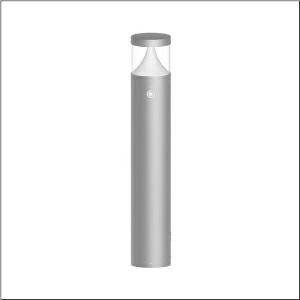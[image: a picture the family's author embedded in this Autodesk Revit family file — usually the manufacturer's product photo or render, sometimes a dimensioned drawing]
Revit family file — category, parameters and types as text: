
# Revit family: cl_31_poller_90_sensor_5cl444803
name_source: partatom
category: Lighting Fixtures
units: mm (PartAtom-declared; Revit-internal decimal feet)

## family parameters
Cut with Voids When Loaded = No
Host = Face
Light Source = No
Part Type = Normal
Room Calculation Point = No
Round Connector Dimension = Use Diameter
Shared = No

## types (1)
- --- (1 x LED, 1500 lm, 14 W, 3000K)
    Apparent Load = 14 VA
    CIE Flux Codes = 19 66 88 92 100
    Color Rendering = 80
    Color Temperature = 3000K
    Default Elevation = 1800 mm
    Description = CL 31 Bollard 90 Sensor, bollard luminaire, primary light control with lens, of PC, primary optical cover: cover panel, of PC, transparent, secondary light control with reflector, of PC, primary light characteristic: asymmetric, LED, rated luminous flux: 1.500lm, luminous efficacy: 107lm/W, light colour: 830, colour temperature: 3000K, control gear: ECG DALI, with terminal, 5-pole, max. 2.5mm², mains connection: 220..240V, AC, 50/60Hz, rated input power: 14W, luminaire housing, of aluminium, powder-coated, Siteco® metallic grey, diameter: 170mm, height: 900mm, PIR sensor, protection rating (complete): IP65, insulation class (complete): insulation class I (protective earthing), certification: CE, ENEC, impact resistance: IK08, permissible operating ambient temperature for outdoor applications: -20..+50°C, packaging unit: 1 piece
    Height = 200 mm  [stored 0.656168 ft]
    Lamp = 1 x LED
    Lamp Light Flux = 1500 lm
    Lamp Power = 14 W
    Lamp count = 1
    Length = 170 mm  [stored 0.557743 ft]
    Luminous efficacy = 107 lm/W
    Manufacturer = Siteco
    ModVariant = No
    Model = 5CL444803
    Mounting Place = Floor
    Mounting Type = Freestanding
    Number of Poles = 1
    OnlyDefault = Yes
    Power Factor = 1
    Product Name = CL 31 Poller 90 Sensor
    Product group = bollard luminaire
    ProductGroupID = 1304
    Protection Class = Protection class I
    Protection Degree = IP 65
    RLX_Detail_Level = 1
    RLX_Emergency_Light_Flux = 0 lm
    RLX_Emergency_Type = 0
    RLX_Emergency_Type_DB = No
    RlxData = <blob elided: 65617 chars, md5=5af5fd18>
    Socket = socket
    Standby Power = 0 W
    System Light Flux = 1500 lm
    System Power = 14 W
    Type Comments = factory setting: luminous flux: 100 % | dim-lin: 254 | 350 mA
    Type Image = l_1006897.jpg
    URL = http://relux.com
    VarID = @adj_130221
    Voltage = 0 V
    Weight = 0.00 kg
    Width = 0 mm  [stored 0 ft]

note: [stored X ft] marks values corroborated as IEEE doubles in the binary element streams (Revit-internal decimal feet)

## geometry (parser evidence)
native form markers: Blend x4, Sweep x9
no freeform markers — native parametric forms only
